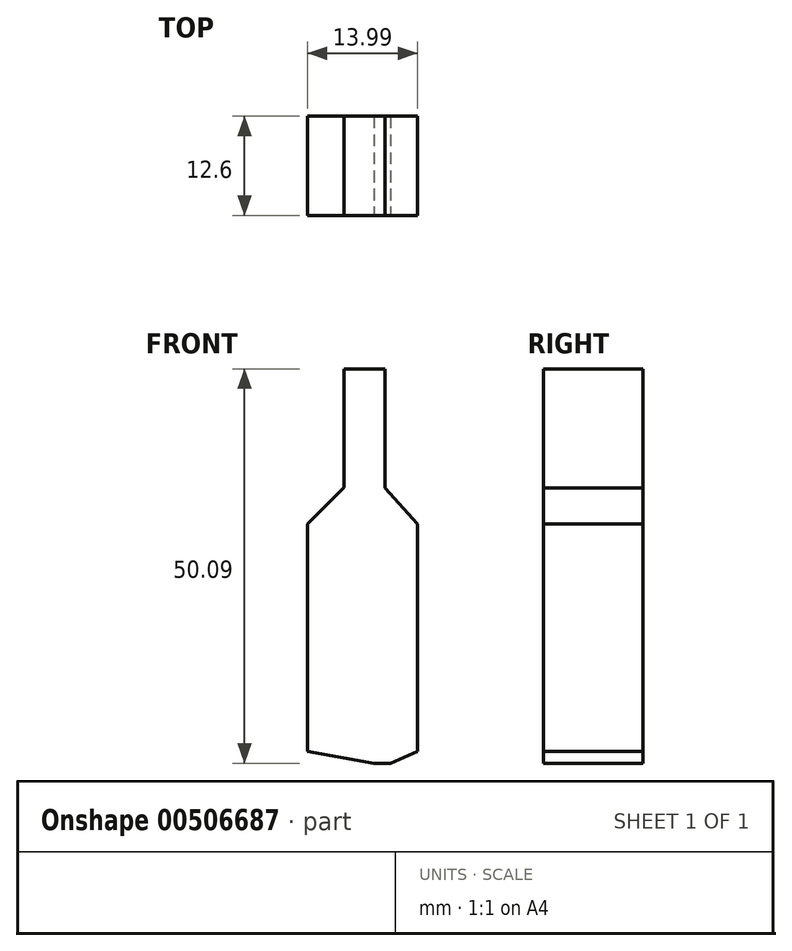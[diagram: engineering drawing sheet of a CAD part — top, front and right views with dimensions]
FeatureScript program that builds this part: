
annotation { "Feature Type Name" : "Feature", "Feature Type Description" : "" }
export const myFeature = defineFeature(function(context is Context, id is Id, definition is map)
    precondition{}
    {
        {
            var Q0;
            Q0=qCreatedBy(makeId("Front.planeOp"),FACE);
            var sketch = newSketch(context, id + "F0", { "sketchPlane" : qUnion([Q0])});
            skLineSegment(sketch, "E0", {"start": v(0, 0) * mm, "end": v(4.2, 0) * mm});
            skLineSegment(sketch, "E1", {"start": v(4.2, 0) * mm, "end": v(7.64, 1.47) * mm});
            skLineSegment(sketch, "E2", {"start": v(7.64, 1.47) * mm, "end": v(7.64, 30.4) * mm});
            skLineSegment(sketch, "E3", {"start": v(7.64, 30.4) * mm, "end": v(3.52, 34.98) * mm});
            skLineSegment(sketch, "E4", {"start": v(3.52, 34.98) * mm, "end": v(3.52, 50.1) * mm});
            skLineSegment(sketch, "E5", {"start": v(3.52, 50.1) * mm, "end": v(-1.73, 50.1) * mm});
            skLineSegment(sketch, "E6", {"start": v(-1.73, 50.1) * mm, "end": v(-1.73, 35.02) * mm});
            skLineSegment(sketch, "E7", {"start": v(-1.73, 35.02) * mm, "end": v(-6.35, 30.4) * mm});
            skLineSegment(sketch, "E8", {"start": v(-6.35, 30.4) * mm, "end": v(-6.35, 1.47) * mm});
            skLineSegment(sketch, "E9", {"start": v(-6.35, 1.47) * mm, "end": v(2.1, 0) * mm});
            skLineSegment(sketch, "E10", {"start": v(2.1, 0) * mm, "end": v(4.2, 0) * mm});
            skSolve(sketch);
        }
        {
            var Q0;
            Q0=makeQuery(id+"F0.imprint","IMPRINT",FACE,{"disambiguationData":[TD([[makeQuery(id+"F0.imprint","IMPRINT",EDGE,{"derivedFrom":sQuery(id+"F0.wireOp",EDGE,"E1")}),1.0]])]});
            extrude(context, id + "F1", {"entities" : qUnion([Q0]), "oppositeDirection" : true, "depth" : 12.6 * mm});
        }
    });
